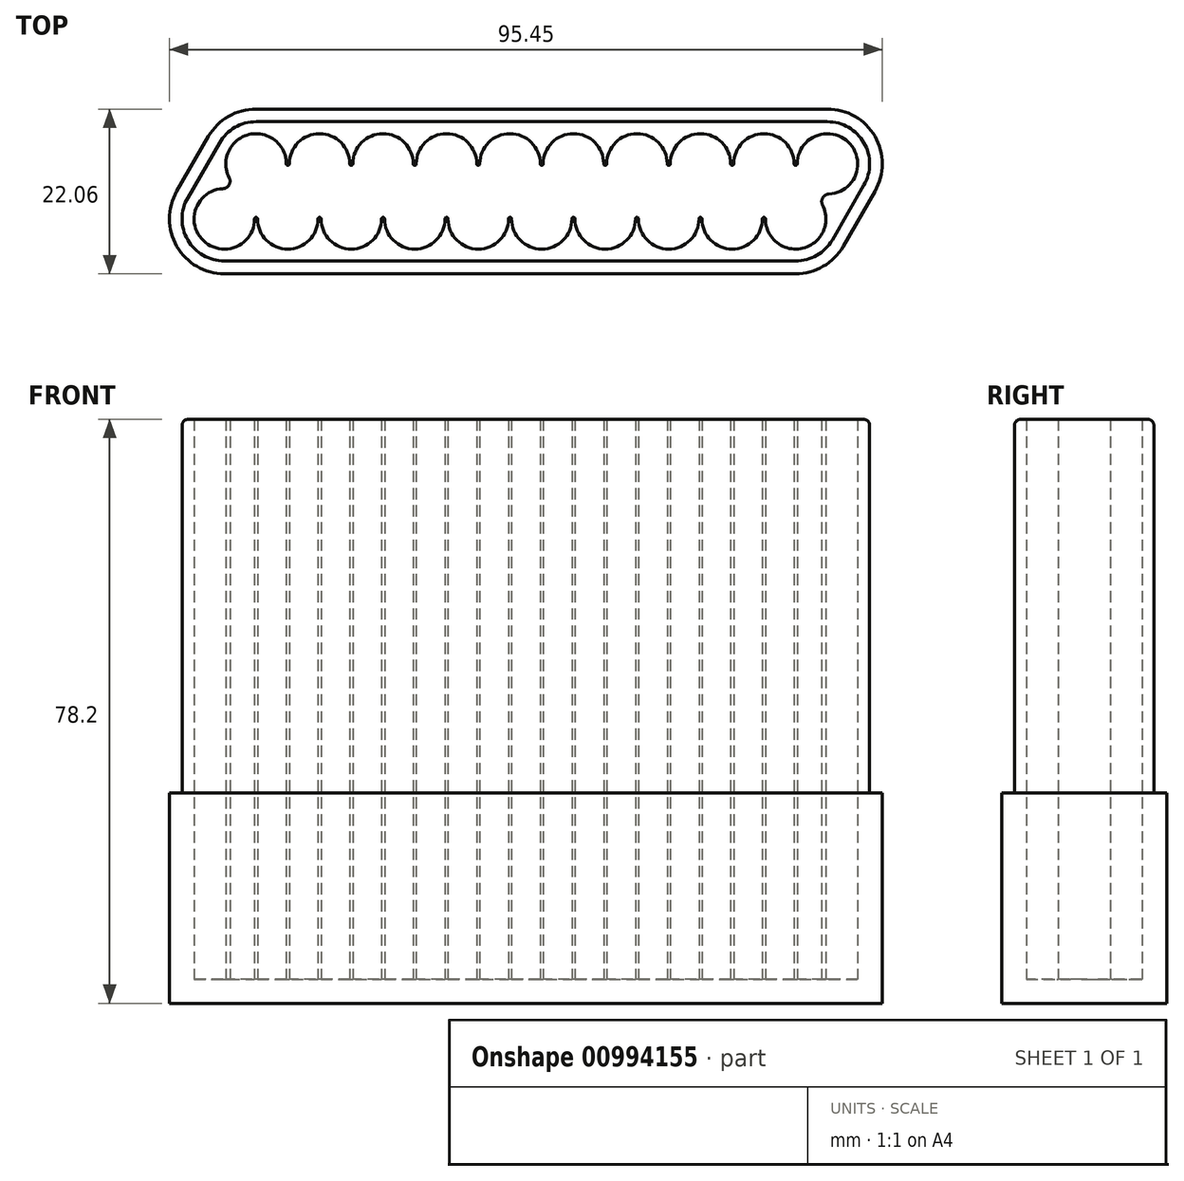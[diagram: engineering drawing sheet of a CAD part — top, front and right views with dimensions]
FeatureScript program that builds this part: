
annotation { "Feature Type Name" : "Feature", "Feature Type Description" : "" }
export const myFeature = defineFeature(function(context is Context, id is Id, definition is map)
    precondition{}
    {
        {
            var Q0;
            Q0=qCreatedBy(makeId("Top.planeOp"),FACE);
            var sketch = newSketch(context, id + "F0", { "sketchPlane" : qUnion([Q0])});
            skCircle(sketch, "E0", {"center": v(0, 0) * mm, "radius": 4.05 * mm});
            skCircle(sketch, "E1.0.1.0", {"center": v(4.25, 7.36) * mm, "radius": 4.05 * mm});
            skCircle(sketch, "E1.1.0.0", {"center": v(8.5, 0) * mm, "radius": 4.05 * mm});
            skCircle(sketch, "E1.1.1.0", {"center": v(12.75, 7.36) * mm, "radius": 4.05 * mm});
            skCircle(sketch, "E1.2.0.0", {"center": v(17, 0) * mm, "radius": 4.05 * mm});
            skCircle(sketch, "E1.2.1.0", {"center": v(21.25, 7.36) * mm, "radius": 4.05 * mm});
            skCircle(sketch, "E1.3.0.0", {"center": v(25.5, 0) * mm, "radius": 4.05 * mm});
            skCircle(sketch, "E1.3.1.0", {"center": v(29.75, 7.36) * mm, "radius": 4.05 * mm});
            skCircle(sketch, "E1.4.0.0", {"center": v(34, 0) * mm, "radius": 4.05 * mm});
            skCircle(sketch, "E1.4.1.0", {"center": v(38.25, 7.36) * mm, "radius": 4.05 * mm});
            skCircle(sketch, "E1.5.0.0", {"center": v(42.5, 0) * mm, "radius": 4.05 * mm});
            skCircle(sketch, "E1.5.1.0", {"center": v(46.75, 7.36) * mm, "radius": 4.05 * mm});
            skCircle(sketch, "E1.6.0.0", {"center": v(51, 0) * mm, "radius": 4.05 * mm});
            skCircle(sketch, "E1.6.1.0", {"center": v(55.25, 7.36) * mm, "radius": 4.05 * mm});
            skCircle(sketch, "E1.7.0.0", {"center": v(59.5, 0) * mm, "radius": 4.05 * mm});
            skCircle(sketch, "E1.7.1.0", {"center": v(63.75, 7.36) * mm, "radius": 4.05 * mm});
            skCircle(sketch, "E1.8.0.0", {"center": v(68, 0) * mm, "radius": 4.05 * mm});
            skCircle(sketch, "E1.8.1.0", {"center": v(72.25, 7.36) * mm, "radius": 4.05 * mm});
            skCircle(sketch, "E1.9.0.0", {"center": v(76.5, 0) * mm, "radius": 4.05 * mm});
            skCircle(sketch, "E1.9.1.0", {"center": v(80.75, 7.36) * mm, "radius": 4.05 * mm});
            skLineSegment(sketch, "E1.direction1", {"start": v(0, 0) * mm, "end": v(8.5, 0) * mm, "construction": true});
            skLineSegment(sketch, "E1.direction2", {"start": v(0, 0) * mm, "end": v(4.25, 7.36) * mm, "construction": true});
            skLineSegment(sketch, "E2", {"start": v(-6.37, 3.67) * mm, "end": v(-2.12, 11.04) * mm});
            skLineSegment(sketch, "E3", {"start": v(-4.9, 2.83) * mm, "end": v(-0.64, 10.19) * mm});
            skLineSegment(sketch, "E4", {"start": v(85.64, 4.54) * mm, "end": v(81.4, -2.82) * mm});
            skLineSegment(sketch, "E5", {"start": v(87.12, 3.69) * mm, "end": v(82.87, -3.67) * mm});
            skLineSegment(sketch, "E6", {"start": v(4.25, 13.01) * mm, "end": v(80.75, 13.01) * mm});
            skLineSegment(sketch, "E7", {"start": v(80.75, 14.71) * mm, "end": v(4.25, 14.71) * mm});
            skLineSegment(sketch, "E8", {"start": v(0, -5.65) * mm, "end": v(76.5, -5.65) * mm});
            skLineSegment(sketch, "E9", {"start": v(76.5, -7.35) * mm, "end": v(0, -7.35) * mm});
            skArc(sketch, "E10", {"start": v(-6.37, 3.67) * mm, "mid": v(-6.37, -3.68) * mm, "end": v(0, -7.35) * mm});
            skArc(sketch, "E11", {"start": v(0, -7.35) * mm, "mid": v(6.37, 3.68) * mm, "end": v(-6.37, 3.67) * mm, "construction": true});
            skArc(sketch, "E12", {"start": v(0, -5.65) * mm, "mid": v(4.9, 2.82) * mm, "end": v(-4.9, 2.83) * mm, "construction": true});
            skArc(sketch, "E13", {"start": v(-4.9, 2.83) * mm, "mid": v(-4.9, -2.83) * mm, "end": v(0, -5.65) * mm});
            skArc(sketch, "E14", {"start": v(4.25, 13.01) * mm, "mid": v(1.43, 12.25) * mm, "end": v(-0.64, 10.19) * mm});
            skArc(sketch, "E15", {"start": v(-0.64, 10.19) * mm, "mid": v(7.08, 2.47) * mm, "end": v(4.25, 13.01) * mm, "construction": true});
            skArc(sketch, "E16", {"start": v(-2.12, 11.04) * mm, "mid": v(7.93, 1) * mm, "end": v(4.25, 14.71) * mm, "construction": true});
            skArc(sketch, "E17", {"start": v(4.25, 14.71) * mm, "mid": v(0.58, 13.73) * mm, "end": v(-2.12, 11.04) * mm});
            skArc(sketch, "E18", {"start": v(80.75, 14.71) * mm, "mid": v(74.38, 3.69) * mm, "end": v(87.12, 3.69) * mm, "construction": true});
            skArc(sketch, "E19", {"start": v(87.12, 3.69) * mm, "mid": v(87.12, 11.04) * mm, "end": v(80.75, 14.71) * mm});
            skArc(sketch, "E20", {"start": v(85.64, 4.54) * mm, "mid": v(85.64, 10.19) * mm, "end": v(80.75, 13.01) * mm});
            skArc(sketch, "E21", {"start": v(80.75, 13.01) * mm, "mid": v(75.86, 4.54) * mm, "end": v(85.64, 4.54) * mm, "construction": true});
            skArc(sketch, "E22", {"start": v(82.87, -3.68) * mm, "mid": v(72.83, 6.37) * mm, "end": v(76.5, -7.35) * mm, "construction": true});
            skArc(sketch, "E23", {"start": v(76.5, -7.35) * mm, "mid": v(80.18, -6.37) * mm, "end": v(82.87, -3.68) * mm});
            skArc(sketch, "E24", {"start": v(76.5, -5.65) * mm, "mid": v(79.33, -4.9) * mm, "end": v(81.4, -2.82) * mm});
            skArc(sketch, "E25", {"start": v(81.4, -2.82) * mm, "mid": v(73.68, 4.9) * mm, "end": v(76.5, -5.65) * mm, "construction": true});
            skArc(sketch, "E26", {"start": v(4.45, 0) * mm, "mid": v(4.25, 0.2) * mm, "end": v(4.05, 0) * mm});
            skArc(sketch, "E27", {"start": v(4.05, 0) * mm, "mid": v(4.25, -0.2) * mm, "end": v(4.45, 0) * mm});
            skArc(sketch, "E28.0.1.0", {"start": v(8.7, 7.36) * mm, "mid": v(8.5, 7.56) * mm, "end": v(8.3, 7.36) * mm});
            skArc(sketch, "E28.0.1.1", {"start": v(8.3, 7.36) * mm, "mid": v(8.5, 7.16) * mm, "end": v(8.7, 7.36) * mm});
            skArc(sketch, "E28.1.0.0", {"start": v(12.95, 0) * mm, "mid": v(12.75, 0.2) * mm, "end": v(12.55, 0) * mm});
            skArc(sketch, "E28.1.0.1", {"start": v(12.55, 0) * mm, "mid": v(12.75, -0.2) * mm, "end": v(12.95, 0) * mm});
            skArc(sketch, "E28.1.1.0", {"start": v(17.2, 7.36) * mm, "mid": v(17, 7.56) * mm, "end": v(16.8, 7.36) * mm});
            skArc(sketch, "E28.1.1.1", {"start": v(16.8, 7.36) * mm, "mid": v(17, 7.16) * mm, "end": v(17.2, 7.36) * mm});
            skArc(sketch, "E28.2.0.0", {"start": v(21.45, 0) * mm, "mid": v(21.25, 0.2) * mm, "end": v(21.05, 0) * mm});
            skArc(sketch, "E28.2.0.1", {"start": v(21.05, 0) * mm, "mid": v(21.25, -0.2) * mm, "end": v(21.45, 0) * mm});
            skArc(sketch, "E28.2.1.0", {"start": v(25.7, 7.36) * mm, "mid": v(25.5, 7.56) * mm, "end": v(25.3, 7.36) * mm});
            skArc(sketch, "E28.2.1.1", {"start": v(25.3, 7.36) * mm, "mid": v(25.5, 7.16) * mm, "end": v(25.7, 7.36) * mm});
            skLineSegment(sketch, "E28.direction1", {"start": v(4.25, 0) * mm, "end": v(12.75, 0) * mm, "construction": true});
            skLineSegment(sketch, "E28.direction2", {"start": v(4.25, 0) * mm, "end": v(8.5, 7.36) * mm, "construction": true});
            skArc(sketch, "E29.0.3.0", {"start": v(29.95, 0) * mm, "mid": v(29.75, 0.2) * mm, "end": v(29.55, 0) * mm});
            skArc(sketch, "E29.4.3.0", {"start": v(29.55, 0) * mm, "mid": v(29.75, -0.2) * mm, "end": v(29.95, 0) * mm});
            skArc(sketch, "E29.0.3.1", {"start": v(34.2, 7.36) * mm, "mid": v(34, 7.56) * mm, "end": v(33.8, 7.36) * mm});
            skArc(sketch, "E29.4.3.1", {"start": v(33.8, 7.36) * mm, "mid": v(34, 7.16) * mm, "end": v(34.2, 7.36) * mm});
            skArc(sketch, "E29.0.4.0", {"start": v(38.45, 0) * mm, "mid": v(38.25, 0.2) * mm, "end": v(38.05, 0) * mm});
            skArc(sketch, "E29.4.4.0", {"start": v(38.05, 0) * mm, "mid": v(38.25, -0.2) * mm, "end": v(38.45, 0) * mm});
            skArc(sketch, "E29.0.4.1", {"start": v(42.7, 7.36) * mm, "mid": v(42.5, 7.56) * mm, "end": v(42.3, 7.36) * mm});
            skArc(sketch, "E29.4.4.1", {"start": v(42.3, 7.36) * mm, "mid": v(42.5, 7.16) * mm, "end": v(42.7, 7.36) * mm});
            skArc(sketch, "E29.0.5.0", {"start": v(46.95, 0) * mm, "mid": v(46.75, 0.2) * mm, "end": v(46.55, 0) * mm});
            skArc(sketch, "E29.4.5.0", {"start": v(46.55, 0) * mm, "mid": v(46.75, -0.2) * mm, "end": v(46.95, 0) * mm});
            skArc(sketch, "E29.0.5.1", {"start": v(51.2, 7.36) * mm, "mid": v(51, 7.56) * mm, "end": v(50.8, 7.36) * mm});
            skArc(sketch, "E29.4.5.1", {"start": v(50.8, 7.36) * mm, "mid": v(51, 7.16) * mm, "end": v(51.2, 7.36) * mm});
            skArc(sketch, "E29.0.6.0", {"start": v(55.45, 0) * mm, "mid": v(55.25, 0.2) * mm, "end": v(55.05, 0) * mm});
            skArc(sketch, "E29.4.6.0", {"start": v(55.05, 0) * mm, "mid": v(55.25, -0.2) * mm, "end": v(55.45, 0) * mm});
            skArc(sketch, "E29.0.6.1", {"start": v(59.7, 7.36) * mm, "mid": v(59.5, 7.56) * mm, "end": v(59.3, 7.36) * mm});
            skArc(sketch, "E29.4.6.1", {"start": v(59.3, 7.36) * mm, "mid": v(59.5, 7.16) * mm, "end": v(59.7, 7.36) * mm});
            skArc(sketch, "E29.0.7.0", {"start": v(63.95, 0) * mm, "mid": v(63.75, 0.2) * mm, "end": v(63.55, 0) * mm});
            skArc(sketch, "E29.4.7.0", {"start": v(63.55, 0) * mm, "mid": v(63.75, -0.2) * mm, "end": v(63.95, 0) * mm});
            skArc(sketch, "E29.0.7.1", {"start": v(68.2, 7.36) * mm, "mid": v(68, 7.56) * mm, "end": v(67.8, 7.36) * mm});
            skArc(sketch, "E29.4.7.1", {"start": v(67.8, 7.36) * mm, "mid": v(68, 7.16) * mm, "end": v(68.2, 7.36) * mm});
            skArc(sketch, "E29.0.8.0", {"start": v(72.45, 0) * mm, "mid": v(72.25, 0.2) * mm, "end": v(72.05, 0) * mm});
            skArc(sketch, "E29.4.8.0", {"start": v(72.05, 0) * mm, "mid": v(72.25, -0.2) * mm, "end": v(72.45, 0) * mm});
            skArc(sketch, "E29.0.8.1", {"start": v(76.7, 7.36) * mm, "mid": v(76.5, 7.56) * mm, "end": v(76.3, 7.36) * mm});
            skArc(sketch, "E29.4.8.1", {"start": v(76.3, 7.36) * mm, "mid": v(76.5, 7.16) * mm, "end": v(76.7, 7.36) * mm});
            skLineSegment(sketch, "E30", {"start": v(76.5, 0) * mm, "end": v(80.75, 7.36) * mm, "construction": true});
            skLineSegment(sketch, "E31", {"start": v(2.13, 3.68) * mm, "end": v(-0.24, 5.04) * mm, "construction": true});
            skArc(sketch, "E32", {"start": v(0.65, 5.5) * mm, "mid": v(-1.1, 5.54) * mm, "end": v(-0.2, 4.05) * mm, "construction": true});
            skArc(sketch, "E33", {"start": v(-0.2, 4.05) * mm, "mid": v(0.63, 4.54) * mm, "end": v(0.65, 5.5) * mm});
            skLineSegment(sketch, "E34", {"start": v(78.62, 3.68) * mm, "end": v(80.99, 2.32) * mm, "construction": true});
            skArc(sketch, "E35", {"start": v(80.94, 3.32) * mm, "mid": v(80.12, 2.82) * mm, "end": v(80.1, 1.86) * mm});
            skArc(sketch, "E36", {"start": v(80.1, 1.86) * mm, "mid": v(81.85, 1.82) * mm, "end": v(80.94, 3.32) * mm, "construction": true});
            skSolve(sketch);
        }
        {
            var Q0;
            Q0=makeQuery(id+"F0.imprint","IMPRINT",FACE,{"disambiguationData":[TD([[makeQuery(id+"F0.imprint","IMPRINT",EDGE,{"derivedFrom":sQuery(id+"F0.wireOp",EDGE,"E3")}),-1.0]])]});
            var Q1;
            Q1=makeQuery(id+"F0.imprint","IMPRINT",FACE,{"disambiguationData":[TD([[makeQuery(id+"F0.imprint","IMPRINT",EDGE,{"derivedFrom":sQuery(id+"F0.wireOp",EDGE,"E26")}),1.0]])]});
            var Q2;
            {var subQ0=sQuery(id+"F0.wireOp",EDGE,"E28.0.1.0");Q2=makeQuery(id+"F0.imprint","IMPRINT",FACE,{"disambiguationData":[TD([[makeQuery(id+"F0.imprint","IMPRINT",EDGE,{"derivedFrom":subQ0}),1.0]])]});}
            var Q3;
            Q3=makeQuery(id+"F0.imprint","IMPRINT",FACE,{"disambiguationData":[TD([[makeQuery(id+"F0.imprint","IMPRINT",EDGE,{"derivedFrom":sQuery(id+"F0.wireOp",EDGE,"E28.1.0.0")}),1.0]])]});
            var Q4;
            Q4=makeQuery(id+"F0.imprint","IMPRINT",FACE,{"disambiguationData":[TD([[makeQuery(id+"F0.imprint","IMPRINT",EDGE,{"derivedFrom":sQuery(id+"F0.wireOp",EDGE,"E28.1.1.0")}),1.0]])]});
            var Q5;
            Q5=makeQuery(id+"F0.imprint","IMPRINT",FACE,{"disambiguationData":[TD([[makeQuery(id+"F0.imprint","IMPRINT",EDGE,{"derivedFrom":sQuery(id+"F0.wireOp",EDGE,"E28.2.0.0")}),1.0]])]});
            var Q6;
            Q6=makeQuery(id+"F0.imprint","IMPRINT",FACE,{"disambiguationData":[TD([[makeQuery(id+"F0.imprint","IMPRINT",EDGE,{"derivedFrom":sQuery(id+"F0.wireOp",EDGE,"E28.2.1.0")}),1.0]])]});
            var Q7;
            Q7=makeQuery(id+"F0.imprint","IMPRINT",FACE,{"disambiguationData":[TD([[makeQuery(id+"F0.imprint","IMPRINT",EDGE,{"derivedFrom":sQuery(id+"F0.wireOp",EDGE,"E29.0.3.0")}),1.0]])]});
            var Q8;
            Q8=makeQuery(id+"F0.imprint","IMPRINT",FACE,{"disambiguationData":[TD([[makeQuery(id+"F0.imprint","IMPRINT",EDGE,{"derivedFrom":sQuery(id+"F0.wireOp",EDGE,"E29.0.3.1")}),1.0]])]});
            var Q9;
            Q9=makeQuery(id+"F0.imprint","IMPRINT",FACE,{"disambiguationData":[TD([[makeQuery(id+"F0.imprint","IMPRINT",EDGE,{"derivedFrom":sQuery(id+"F0.wireOp",EDGE,"E29.0.4.0")}),1.0]])]});
            var Q10;
            Q10=makeQuery(id+"F0.imprint","IMPRINT",FACE,{"disambiguationData":[TD([[makeQuery(id+"F0.imprint","IMPRINT",EDGE,{"derivedFrom":sQuery(id+"F0.wireOp",EDGE,"E29.0.4.1")}),1.0]])]});
            var Q11;
            Q11=makeQuery(id+"F0.imprint","IMPRINT",FACE,{"disambiguationData":[TD([[makeQuery(id+"F0.imprint","IMPRINT",EDGE,{"derivedFrom":sQuery(id+"F0.wireOp",EDGE,"E29.0.5.0")}),1.0]])]});
            var Q12;
            Q12=makeQuery(id+"F0.imprint","IMPRINT",FACE,{"disambiguationData":[TD([[makeQuery(id+"F0.imprint","IMPRINT",EDGE,{"derivedFrom":sQuery(id+"F0.wireOp",EDGE,"E29.0.5.1")}),1.0]])]});
            var Q13;
            Q13=makeQuery(id+"F0.imprint","IMPRINT",FACE,{"disambiguationData":[TD([[makeQuery(id+"F0.imprint","IMPRINT",EDGE,{"derivedFrom":sQuery(id+"F0.wireOp",EDGE,"E29.0.6.0")}),1.0]])]});
            var Q14;
            Q14=makeQuery(id+"F0.imprint","IMPRINT",FACE,{"disambiguationData":[TD([[makeQuery(id+"F0.imprint","IMPRINT",EDGE,{"derivedFrom":sQuery(id+"F0.wireOp",EDGE,"E29.0.6.1")}),1.0]])]});
            var Q15;
            Q15=makeQuery(id+"F0.imprint","IMPRINT",FACE,{"disambiguationData":[TD([[makeQuery(id+"F0.imprint","IMPRINT",EDGE,{"derivedFrom":sQuery(id+"F0.wireOp",EDGE,"E29.0.7.0")}),1.0]])]});
            var Q16;
            Q16=makeQuery(id+"F0.imprint","IMPRINT",FACE,{"disambiguationData":[TD([[makeQuery(id+"F0.imprint","IMPRINT",EDGE,{"derivedFrom":sQuery(id+"F0.wireOp",EDGE,"E29.0.7.1")}),1.0]])]});
            var Q17;
            Q17=makeQuery(id+"F0.imprint","IMPRINT",FACE,{"disambiguationData":[TD([[makeQuery(id+"F0.imprint","IMPRINT",EDGE,{"derivedFrom":sQuery(id+"F0.wireOp",EDGE,"E29.0.8.0")}),1.0]])]});
            var Q18;
            Q18=makeQuery(id+"F0.imprint","IMPRINT",FACE,{"disambiguationData":[TD([[makeQuery(id+"F0.imprint","IMPRINT",EDGE,{"derivedFrom":sQuery(id+"F0.wireOp",EDGE,"E29.0.8.1")}),1.0]])]});
            var Q19;
            Q19=makeQuery(id+"F0.imprint","IMPRINT",FACE,{"disambiguationData":[TD([[makeQuery(id+"F0.imprint","IMPRINT",EDGE,{"derivedFrom":sQuery(id+"F0.wireOp",EDGE,"E29.0.9.0")}),1.0]])]});
            var Q20;
            Q20=makeQuery(id+"F0.imprint","IMPRINT",FACE,{"disambiguationData":[TD([[makeQuery(id+"F0.imprint","IMPRINT",EDGE,{"derivedFrom":sQuery(id+"F0.wireOp",EDGE,"E29.0.9.1")}),1.0]])]});
            var Q21;
            Q21=makeQuery(id+"F0.imprint","IMPRINT",FACE,{"disambiguationData":[TD([[makeQuery(id+"F0.imprint","IMPRINT",EDGE,{"derivedFrom":sQuery(id+"F0.wireOp",EDGE,"E29.0.10.0")}),1.0]])]});
            var Q22;
            Q22=makeQuery(id+"F0.imprint","IMPRINT",FACE,{"disambiguationData":[TD([[makeQuery(id+"F0.imprint","IMPRINT",EDGE,{"derivedFrom":sQuery(id+"F0.wireOp",EDGE,"E29.0.10.1")}),1.0]])]});
            var Q23;
            Q23=makeQuery(id+"F0.imprint","IMPRINT",FACE,{"disambiguationData":[TD([[makeQuery(id+"F0.imprint","IMPRINT",EDGE,{"derivedFrom":sQuery(id+"F0.wireOp",EDGE,"E29.0.11.0")}),1.0]])]});
            var Q24;
            Q24=makeQuery(id+"F0.imprint","IMPRINT",FACE,{"disambiguationData":[TD([[makeQuery(id+"F0.imprint","IMPRINT",EDGE,{"derivedFrom":sQuery(id+"F0.wireOp",EDGE,"E29.0.11.1")}),1.0]])]});
            var Q25;
            Q25=makeQuery(id+"F0.imprint","IMPRINT",FACE,{"disambiguationData":[TD([[makeQuery(id+"F0.imprint","IMPRINT",EDGE,{"derivedFrom":sQuery(id+"F0.wireOp",EDGE,"E29.0.12.0")}),1.0]])]});
            var Q26;
            Q26=makeQuery(id+"F0.imprint","IMPRINT",FACE,{"disambiguationData":[TD([[makeQuery(id+"F0.imprint","IMPRINT",EDGE,{"derivedFrom":sQuery(id+"F0.wireOp",EDGE,"E29.0.12.1")}),1.0]])]});
            var Q27;
            Q27=makeQuery(id+"F0.imprint","IMPRINT",FACE,{"disambiguationData":[TD([[makeQuery(id+"F0.imprint","IMPRINT",EDGE,{"derivedFrom":sQuery(id+"F0.wireOp",EDGE,"E29.0.13.0")}),1.0]])]});
            var Q28;
            Q28=makeQuery(id+"F0.imprint","IMPRINT",FACE,{"disambiguationData":[TD([[makeQuery(id+"F0.imprint","IMPRINT",EDGE,{"derivedFrom":sQuery(id+"F0.wireOp",EDGE,"E29.0.13.1")}),1.0]])]});
            var Q29;
            Q29=makeQuery(id+"F0.imprint","IMPRINT",FACE,{"disambiguationData":[TD([[makeQuery(id+"F0.imprint","IMPRINT",EDGE,{"derivedFrom":sQuery(id+"F0.wireOp",EDGE,"E29.0.14.0")}),1.0]])]});
            var Q30;
            Q30=makeQuery(id+"F0.imprint","IMPRINT",FACE,{"disambiguationData":[TD([[makeQuery(id+"F0.imprint","IMPRINT",EDGE,{"derivedFrom":sQuery(id+"F0.wireOp",EDGE,"E29.0.14.1")}),1.0]])]});
            var Q31;
            Q31=makeQuery(id+"F0.imprint","IMPRINT",FACE,{"disambiguationData":[TD([[makeQuery(id+"F0.imprint","IMPRINT",EDGE,{"derivedFrom":sQuery(id+"F0.wireOp",EDGE,"E29.0.15.0")}),1.0]])]});
            var Q32;
            Q32=makeQuery(id+"F0.imprint","IMPRINT",FACE,{"disambiguationData":[TD([[makeQuery(id+"F0.imprint","IMPRINT",EDGE,{"derivedFrom":sQuery(id+"F0.wireOp",EDGE,"E29.0.15.1")}),1.0]])]});
            var Q33;
            Q33=makeQuery(id+"F0.imprint","IMPRINT",FACE,{"disambiguationData":[TD([[makeQuery(id+"F0.imprint","IMPRINT",EDGE,{"derivedFrom":sQuery(id+"F0.wireOp",EDGE,"E29.0.16.0")}),1.0]])]});
            var Q34;
            Q34=makeQuery(id+"F0.imprint","IMPRINT",FACE,{"disambiguationData":[TD([[makeQuery(id+"F0.imprint","IMPRINT",EDGE,{"derivedFrom":sQuery(id+"F0.wireOp",EDGE,"E29.0.16.1")}),1.0]])]});
            var Q35;
            Q35=makeQuery(id+"F0.imprint","IMPRINT",FACE,{"disambiguationData":[TD([[makeQuery(id+"F0.imprint","IMPRINT",EDGE,{"derivedFrom":sQuery(id+"F0.wireOp",EDGE,"E29.0.17.0")}),1.0]])]});
            var Q36;
            Q36=makeQuery(id+"F0.imprint","IMPRINT",FACE,{"disambiguationData":[TD([[makeQuery(id+"F0.imprint","IMPRINT",EDGE,{"derivedFrom":sQuery(id+"F0.wireOp",EDGE,"E29.0.17.1")}),1.0]])]});
            var Q37;
            Q37=makeQuery(id+"F0.imprint","IMPRINT",FACE,{"disambiguationData":[TD([[makeQuery(id+"F0.imprint","IMPRINT",EDGE,{"derivedFrom":sQuery(id+"F0.wireOp",EDGE,"E29.0.18.0")}),1.0]])]});
            var Q38;
            Q38=makeQuery(id+"F0.imprint","IMPRINT",FACE,{"disambiguationData":[TD([[makeQuery(id+"F0.imprint","IMPRINT",EDGE,{"derivedFrom":sQuery(id+"F0.wireOp",EDGE,"E29.0.18.1")}),1.0]])]});
            extrude(context, id + "F1", {"entities" : qUnion([Q0, Q1, Q2, Q3, Q4, Q5, Q6, Q7, Q8, Q9, Q10, Q11, Q12, Q13, Q14, Q15, Q16, Q17, Q18, Q19, Q20, Q21, Q22, Q23, Q24, Q25, Q26, Q27, Q28, Q29, Q30, Q31, Q32, Q33, Q34, Q35, Q36, Q37, Q38]), "depth" : 75 * mm, "offsetDistance" : 25 * mm});
        }
        {
            var Q0;
            Q0=makeQuery(id+"F0.imprint","IMPRINT",FACE,{"disambiguationData":[TD([[makeQuery(id+"F0.imprint","IMPRINT",EDGE,{"derivedFrom":sQuery(id+"F0.wireOp",EDGE,"a81a9441-913f-4e04-ae89-87223a70fdbe.0")}),1.0]])]});
            var Q1;
            Q1=makeQuery(id+"F0.imprint","IMPRINT",FACE,{"disambiguationData":[TD([[makeQuery(id+"F0.imprint","IMPRINT",EDGE,{"derivedFrom":sQuery(id+"F0.wireOp",EDGE,"E2")}),-1.0]])]});
            extrude(context, id + "F2", {"entities" : qUnion([Q0, Q1]), "operationType" : NewBodyOperationType.ADD, "depth" : 25 * mm, "offsetDistance" : 25 * mm});
        }
        {
            var Q0;
            Q0=qSketchRegion(id+"F0",true);
            var Q1;
            Q1=makeQuery(id+"F0.imprint","IMPRINT",FACE,{"disambiguationData":[TD([[makeQuery(id+"F0.imprint","IMPRINT",EDGE,{"derivedFrom":sQuery(id+"F0.wireOp",EDGE,"E3")}),-1.0]])]});
            var Q2;
            {var subQ50=sQuery(id+"F0.wireOp",EDGE,"f7ba4f12-d8f7-416d-8bb5-9bc70fdc84212");Q2=makeQuery(id+"F0.imprint","IMPRINT",FACE,{"disambiguationData":[TD([[makeQuery(id+"F0.imprint","IMPRINT",EDGE,{"derivedFrom":subQ50}),-1.0]])]});}
            var Q3;
            {var subQ0=sQuery(id+"F0.wireOp",EDGE,"E0");var subQ1=makeQuery(id+"F0.imprint","INTERSECT",VERTEX,{"derivedFrom":[subQ0,sQuery(id+"F0.wireOp",EDGE,"f7ba4f12-d8f7-416d-8bb5-9bc70fdc84212")]});Q3=makeQuery(id+"F0.imprint","IMPRINT",FACE,{"disambiguationData":[TD([[makeQuery(id+"F0.imprint","IMPRINT",EDGE,{"disambiguationData":[TD([[subQ1,1.0]])],"derivedFrom":subQ0}),1.0]])]});}
            var Q4;
            {var subQ0=sQuery(id+"F0.wireOp",EDGE,"E1.0.1.0");var subQ1=makeQuery(id+"F0.imprint","INTERSECT",VERTEX,{"derivedFrom":[subQ0,sQuery(id+"F0.wireOp",EDGE,"f7ba4f12-d8f7-416d-8bb5-9bc70fdc84212")]});Q4=makeQuery(id+"F0.imprint","IMPRINT",FACE,{"disambiguationData":[TD([[makeQuery(id+"F0.imprint","IMPRINT",EDGE,{"disambiguationData":[TD([[subQ1,1.0]])],"derivedFrom":subQ0}),1.0]])]});}
            var Q5;
            {var subQ0=sQuery(id+"F0.wireOp",EDGE,"E1.1.0.0");var subQ1=makeQuery(id+"F0.imprint","INTERSECT",VERTEX,{"derivedFrom":[subQ0,sQuery(id+"F0.wireOp",EDGE,"E26")]});Q5=makeQuery(id+"F0.imprint","IMPRINT",FACE,{"disambiguationData":[TD([[makeQuery(id+"F0.imprint","IMPRINT",EDGE,{"disambiguationData":[TD([[subQ1,1.0]])],"derivedFrom":subQ0}),1.0]])]});}
            var Q6;
            {var subQ0=sQuery(id+"F0.wireOp",EDGE,"E1.1.1.0");var subQ1=makeQuery(id+"F0.imprint","INTERSECT",VERTEX,{"derivedFrom":[subQ0,sQuery(id+"F0.wireOp",EDGE,"E28.0.1.1")]});Q6=makeQuery(id+"F0.imprint","IMPRINT",FACE,{"disambiguationData":[TD([[makeQuery(id+"F0.imprint","IMPRINT",EDGE,{"disambiguationData":[TD([[subQ1,1.0]])],"derivedFrom":subQ0}),1.0]])]});}
            var Q7;
            {var subQ0=sQuery(id+"F0.wireOp",EDGE,"E1.2.0.0");var subQ1=makeQuery(id+"F0.imprint","INTERSECT",VERTEX,{"derivedFrom":[subQ0,sQuery(id+"F0.wireOp",EDGE,"E28.1.0.0")]});Q7=makeQuery(id+"F0.imprint","IMPRINT",FACE,{"disambiguationData":[TD([[makeQuery(id+"F0.imprint","IMPRINT",EDGE,{"disambiguationData":[TD([[subQ1,1.0]])],"derivedFrom":subQ0}),1.0]])]});}
            var Q8;
            {var subQ0=sQuery(id+"F0.wireOp",EDGE,"E1.2.1.0");var subQ1=makeQuery(id+"F0.imprint","INTERSECT",VERTEX,{"derivedFrom":[subQ0,sQuery(id+"F0.wireOp",EDGE,"E28.1.1.1")]});Q8=makeQuery(id+"F0.imprint","IMPRINT",FACE,{"disambiguationData":[TD([[makeQuery(id+"F0.imprint","IMPRINT",EDGE,{"disambiguationData":[TD([[subQ1,1.0]])],"derivedFrom":subQ0}),1.0]])]});}
            var Q9;
            {var subQ0=sQuery(id+"F0.wireOp",EDGE,"E1.3.0.0");var subQ1=makeQuery(id+"F0.imprint","INTERSECT",VERTEX,{"derivedFrom":[subQ0,sQuery(id+"F0.wireOp",EDGE,"E28.2.0.0")]});Q9=makeQuery(id+"F0.imprint","IMPRINT",FACE,{"disambiguationData":[TD([[makeQuery(id+"F0.imprint","IMPRINT",EDGE,{"disambiguationData":[TD([[subQ1,1.0]])],"derivedFrom":subQ0}),1.0]])]});}
            var Q10;
            {var subQ0=sQuery(id+"F0.wireOp",EDGE,"E1.3.1.0");var subQ1=makeQuery(id+"F0.imprint","INTERSECT",VERTEX,{"derivedFrom":[subQ0,sQuery(id+"F0.wireOp",EDGE,"E28.2.1.1")]});Q10=makeQuery(id+"F0.imprint","IMPRINT",FACE,{"disambiguationData":[TD([[makeQuery(id+"F0.imprint","IMPRINT",EDGE,{"disambiguationData":[TD([[subQ1,1.0]])],"derivedFrom":subQ0}),1.0]])]});}
            var Q11;
            {var subQ0=sQuery(id+"F0.wireOp",EDGE,"E1.4.0.0");var subQ1=makeQuery(id+"F0.imprint","INTERSECT",VERTEX,{"derivedFrom":[subQ0,sQuery(id+"F0.wireOp",EDGE,"E29.0.3.0")]});Q11=makeQuery(id+"F0.imprint","IMPRINT",FACE,{"disambiguationData":[TD([[makeQuery(id+"F0.imprint","IMPRINT",EDGE,{"disambiguationData":[TD([[subQ1,1.0]])],"derivedFrom":subQ0}),1.0]])]});}
            var Q12;
            {var subQ0=sQuery(id+"F0.wireOp",EDGE,"E1.4.1.0");var subQ1=makeQuery(id+"F0.imprint","INTERSECT",VERTEX,{"derivedFrom":[subQ0,sQuery(id+"F0.wireOp",EDGE,"E29.4.3.1")]});Q12=makeQuery(id+"F0.imprint","IMPRINT",FACE,{"disambiguationData":[TD([[makeQuery(id+"F0.imprint","IMPRINT",EDGE,{"disambiguationData":[TD([[subQ1,1.0]])],"derivedFrom":subQ0}),1.0]])]});}
            var Q13;
            {var subQ0=sQuery(id+"F0.wireOp",EDGE,"E1.5.0.0");var subQ1=makeQuery(id+"F0.imprint","INTERSECT",VERTEX,{"derivedFrom":[subQ0,sQuery(id+"F0.wireOp",EDGE,"E29.0.4.0")]});Q13=makeQuery(id+"F0.imprint","IMPRINT",FACE,{"disambiguationData":[TD([[makeQuery(id+"F0.imprint","IMPRINT",EDGE,{"disambiguationData":[TD([[subQ1,1.0]])],"derivedFrom":subQ0}),1.0]])]});}
            var Q14;
            {var subQ0=sQuery(id+"F0.wireOp",EDGE,"E1.5.1.0");var subQ1=makeQuery(id+"F0.imprint","INTERSECT",VERTEX,{"derivedFrom":[subQ0,sQuery(id+"F0.wireOp",EDGE,"E29.4.4.1")]});Q14=makeQuery(id+"F0.imprint","IMPRINT",FACE,{"disambiguationData":[TD([[makeQuery(id+"F0.imprint","IMPRINT",EDGE,{"disambiguationData":[TD([[subQ1,1.0]])],"derivedFrom":subQ0}),1.0]])]});}
            var Q15;
            {var subQ0=sQuery(id+"F0.wireOp",EDGE,"E1.6.0.0");var subQ1=makeQuery(id+"F0.imprint","INTERSECT",VERTEX,{"derivedFrom":[subQ0,sQuery(id+"F0.wireOp",EDGE,"E29.0.5.0")]});Q15=makeQuery(id+"F0.imprint","IMPRINT",FACE,{"disambiguationData":[TD([[makeQuery(id+"F0.imprint","IMPRINT",EDGE,{"disambiguationData":[TD([[subQ1,1.0]])],"derivedFrom":subQ0}),1.0]])]});}
            var Q16;
            {var subQ0=sQuery(id+"F0.wireOp",EDGE,"E1.6.1.0");var subQ1=makeQuery(id+"F0.imprint","INTERSECT",VERTEX,{"derivedFrom":[subQ0,sQuery(id+"F0.wireOp",EDGE,"E29.4.5.1")]});Q16=makeQuery(id+"F0.imprint","IMPRINT",FACE,{"disambiguationData":[TD([[makeQuery(id+"F0.imprint","IMPRINT",EDGE,{"disambiguationData":[TD([[subQ1,1.0]])],"derivedFrom":subQ0}),1.0]])]});}
            var Q17;
            {var subQ0=sQuery(id+"F0.wireOp",EDGE,"E1.7.0.0");var subQ1=makeQuery(id+"F0.imprint","INTERSECT",VERTEX,{"derivedFrom":[subQ0,sQuery(id+"F0.wireOp",EDGE,"E29.0.6.0")]});Q17=makeQuery(id+"F0.imprint","IMPRINT",FACE,{"disambiguationData":[TD([[makeQuery(id+"F0.imprint","IMPRINT",EDGE,{"disambiguationData":[TD([[subQ1,1.0]])],"derivedFrom":subQ0}),1.0]])]});}
            var Q18;
            {var subQ0=sQuery(id+"F0.wireOp",EDGE,"E1.7.1.0");var subQ1=makeQuery(id+"F0.imprint","INTERSECT",VERTEX,{"derivedFrom":[subQ0,sQuery(id+"F0.wireOp",EDGE,"E29.4.6.1")]});Q18=makeQuery(id+"F0.imprint","IMPRINT",FACE,{"disambiguationData":[TD([[makeQuery(id+"F0.imprint","IMPRINT",EDGE,{"disambiguationData":[TD([[subQ1,1.0]])],"derivedFrom":subQ0}),1.0]])]});}
            var Q19;
            {var subQ0=sQuery(id+"F0.wireOp",EDGE,"E1.8.0.0");var subQ1=makeQuery(id+"F0.imprint","INTERSECT",VERTEX,{"derivedFrom":[subQ0,sQuery(id+"F0.wireOp",EDGE,"E29.0.7.0")]});Q19=makeQuery(id+"F0.imprint","IMPRINT",FACE,{"disambiguationData":[TD([[makeQuery(id+"F0.imprint","IMPRINT",EDGE,{"disambiguationData":[TD([[subQ1,1.0]])],"derivedFrom":subQ0}),1.0]])]});}
            var Q20;
            {var subQ0=sQuery(id+"F0.wireOp",EDGE,"E1.8.1.0");var subQ1=makeQuery(id+"F0.imprint","INTERSECT",VERTEX,{"derivedFrom":[subQ0,sQuery(id+"F0.wireOp",EDGE,"E29.4.7.1")]});Q20=makeQuery(id+"F0.imprint","IMPRINT",FACE,{"disambiguationData":[TD([[makeQuery(id+"F0.imprint","IMPRINT",EDGE,{"disambiguationData":[TD([[subQ1,1.0]])],"derivedFrom":subQ0}),1.0]])]});}
            var Q21;
            {var subQ0=sQuery(id+"F0.wireOp",EDGE,"E1.9.0.0");var subQ1=makeQuery(id+"F0.imprint","INTERSECT",VERTEX,{"derivedFrom":[subQ0,sQuery(id+"F0.wireOp",EDGE,"E29.0.8.0")]});Q21=makeQuery(id+"F0.imprint","IMPRINT",FACE,{"disambiguationData":[TD([[makeQuery(id+"F0.imprint","IMPRINT",EDGE,{"disambiguationData":[TD([[subQ1,1.0]])],"derivedFrom":subQ0}),1.0]])]});}
            var Q22;
            {var subQ0=sQuery(id+"F0.wireOp",EDGE,"E1.9.1.0");var subQ1=makeQuery(id+"F0.imprint","INTERSECT",VERTEX,{"derivedFrom":[subQ0,sQuery(id+"F0.wireOp",EDGE,"E29.4.8.1")]});Q22=makeQuery(id+"F0.imprint","IMPRINT",FACE,{"disambiguationData":[TD([[makeQuery(id+"F0.imprint","IMPRINT",EDGE,{"disambiguationData":[TD([[subQ1,1.0]])],"derivedFrom":subQ0}),1.0]])]});}
            var Q23;
            {var subQ0=sQuery(id+"F0.wireOp",EDGE,"bb5cbe6f-1803-4565-ad2e-bfdc8dac2585.0.10.0");var subQ1=makeQuery(id+"F0.imprint","INTERSECT",VERTEX,{"derivedFrom":[subQ0,sQuery(id+"F0.wireOp",EDGE,"E29.0.9.0")]});Q23=makeQuery(id+"F0.imprint","IMPRINT",FACE,{"disambiguationData":[TD([[makeQuery(id+"F0.imprint","IMPRINT",EDGE,{"disambiguationData":[TD([[subQ1,1.0]])],"derivedFrom":subQ0}),1.0]])]});}
            var Q24;
            {var subQ0=sQuery(id+"F0.wireOp",EDGE,"bb5cbe6f-1803-4565-ad2e-bfdc8dac2585.0.10.1");var subQ1=makeQuery(id+"F0.imprint","INTERSECT",VERTEX,{"derivedFrom":[subQ0,sQuery(id+"F0.wireOp",EDGE,"E29.4.9.1")]});Q24=makeQuery(id+"F0.imprint","IMPRINT",FACE,{"disambiguationData":[TD([[makeQuery(id+"F0.imprint","IMPRINT",EDGE,{"disambiguationData":[TD([[subQ1,1.0]])],"derivedFrom":subQ0}),1.0]])]});}
            var Q25;
            {var subQ0=sQuery(id+"F0.wireOp",EDGE,"bb5cbe6f-1803-4565-ad2e-bfdc8dac2585.0.11.0");var subQ1=makeQuery(id+"F0.imprint","INTERSECT",VERTEX,{"derivedFrom":[subQ0,sQuery(id+"F0.wireOp",EDGE,"E29.0.10.0")]});Q25=makeQuery(id+"F0.imprint","IMPRINT",FACE,{"disambiguationData":[TD([[makeQuery(id+"F0.imprint","IMPRINT",EDGE,{"disambiguationData":[TD([[subQ1,1.0]])],"derivedFrom":subQ0}),1.0]])]});}
            var Q26;
            {var subQ0=sQuery(id+"F0.wireOp",EDGE,"bb5cbe6f-1803-4565-ad2e-bfdc8dac2585.0.11.1");var subQ1=makeQuery(id+"F0.imprint","INTERSECT",VERTEX,{"derivedFrom":[subQ0,sQuery(id+"F0.wireOp",EDGE,"E29.4.10.1")]});Q26=makeQuery(id+"F0.imprint","IMPRINT",FACE,{"disambiguationData":[TD([[makeQuery(id+"F0.imprint","IMPRINT",EDGE,{"disambiguationData":[TD([[subQ1,1.0]])],"derivedFrom":subQ0}),1.0]])]});}
            var Q27;
            {var subQ0=sQuery(id+"F0.wireOp",EDGE,"bb5cbe6f-1803-4565-ad2e-bfdc8dac2585.0.12.0");var subQ1=makeQuery(id+"F0.imprint","INTERSECT",VERTEX,{"derivedFrom":[subQ0,sQuery(id+"F0.wireOp",EDGE,"E29.0.11.0")]});Q27=makeQuery(id+"F0.imprint","IMPRINT",FACE,{"disambiguationData":[TD([[makeQuery(id+"F0.imprint","IMPRINT",EDGE,{"disambiguationData":[TD([[subQ1,1.0]])],"derivedFrom":subQ0}),1.0]])]});}
            var Q28;
            {var subQ0=sQuery(id+"F0.wireOp",EDGE,"bb5cbe6f-1803-4565-ad2e-bfdc8dac2585.0.12.1");var subQ1=makeQuery(id+"F0.imprint","INTERSECT",VERTEX,{"derivedFrom":[subQ0,sQuery(id+"F0.wireOp",EDGE,"E29.4.11.1")]});Q28=makeQuery(id+"F0.imprint","IMPRINT",FACE,{"disambiguationData":[TD([[makeQuery(id+"F0.imprint","IMPRINT",EDGE,{"disambiguationData":[TD([[subQ1,1.0]])],"derivedFrom":subQ0}),1.0]])]});}
            var Q29;
            {var subQ0=sQuery(id+"F0.wireOp",EDGE,"bb5cbe6f-1803-4565-ad2e-bfdc8dac2585.0.13.0");var subQ1=makeQuery(id+"F0.imprint","INTERSECT",VERTEX,{"derivedFrom":[subQ0,sQuery(id+"F0.wireOp",EDGE,"E29.0.12.0")]});Q29=makeQuery(id+"F0.imprint","IMPRINT",FACE,{"disambiguationData":[TD([[makeQuery(id+"F0.imprint","IMPRINT",EDGE,{"disambiguationData":[TD([[subQ1,1.0]])],"derivedFrom":subQ0}),1.0]])]});}
            var Q30;
            {var subQ0=sQuery(id+"F0.wireOp",EDGE,"bb5cbe6f-1803-4565-ad2e-bfdc8dac2585.0.13.1");var subQ1=makeQuery(id+"F0.imprint","INTERSECT",VERTEX,{"derivedFrom":[subQ0,sQuery(id+"F0.wireOp",EDGE,"E29.4.12.1")]});Q30=makeQuery(id+"F0.imprint","IMPRINT",FACE,{"disambiguationData":[TD([[makeQuery(id+"F0.imprint","IMPRINT",EDGE,{"disambiguationData":[TD([[subQ1,1.0]])],"derivedFrom":subQ0}),1.0]])]});}
            var Q31;
            {var subQ0=sQuery(id+"F0.wireOp",EDGE,"bb5cbe6f-1803-4565-ad2e-bfdc8dac2585.0.14.0");var subQ1=makeQuery(id+"F0.imprint","INTERSECT",VERTEX,{"derivedFrom":[subQ0,sQuery(id+"F0.wireOp",EDGE,"E29.0.13.0")]});Q31=makeQuery(id+"F0.imprint","IMPRINT",FACE,{"disambiguationData":[TD([[makeQuery(id+"F0.imprint","IMPRINT",EDGE,{"disambiguationData":[TD([[subQ1,1.0]])],"derivedFrom":subQ0}),1.0]])]});}
            var Q32;
            {var subQ0=sQuery(id+"F0.wireOp",EDGE,"bb5cbe6f-1803-4565-ad2e-bfdc8dac2585.0.14.1");var subQ1=makeQuery(id+"F0.imprint","INTERSECT",VERTEX,{"derivedFrom":[subQ0,sQuery(id+"F0.wireOp",EDGE,"E29.4.13.1")]});Q32=makeQuery(id+"F0.imprint","IMPRINT",FACE,{"disambiguationData":[TD([[makeQuery(id+"F0.imprint","IMPRINT",EDGE,{"disambiguationData":[TD([[subQ1,1.0]])],"derivedFrom":subQ0}),1.0]])]});}
            var Q33;
            {var subQ0=sQuery(id+"F0.wireOp",EDGE,"bb5cbe6f-1803-4565-ad2e-bfdc8dac2585.0.15.0");var subQ1=makeQuery(id+"F0.imprint","INTERSECT",VERTEX,{"derivedFrom":[subQ0,sQuery(id+"F0.wireOp",EDGE,"E29.0.14.0")]});Q33=makeQuery(id+"F0.imprint","IMPRINT",FACE,{"disambiguationData":[TD([[makeQuery(id+"F0.imprint","IMPRINT",EDGE,{"disambiguationData":[TD([[subQ1,1.0]])],"derivedFrom":subQ0}),1.0]])]});}
            var Q34;
            {var subQ0=sQuery(id+"F0.wireOp",EDGE,"bb5cbe6f-1803-4565-ad2e-bfdc8dac2585.0.15.1");var subQ1=makeQuery(id+"F0.imprint","INTERSECT",VERTEX,{"derivedFrom":[subQ0,sQuery(id+"F0.wireOp",EDGE,"E29.4.14.1")]});Q34=makeQuery(id+"F0.imprint","IMPRINT",FACE,{"disambiguationData":[TD([[makeQuery(id+"F0.imprint","IMPRINT",EDGE,{"disambiguationData":[TD([[subQ1,1.0]])],"derivedFrom":subQ0}),1.0]])]});}
            var Q35;
            {var subQ0=sQuery(id+"F0.wireOp",EDGE,"bb5cbe6f-1803-4565-ad2e-bfdc8dac2585.0.16.0");var subQ1=makeQuery(id+"F0.imprint","INTERSECT",VERTEX,{"derivedFrom":[subQ0,sQuery(id+"F0.wireOp",EDGE,"E29.0.15.0")]});Q35=makeQuery(id+"F0.imprint","IMPRINT",FACE,{"disambiguationData":[TD([[makeQuery(id+"F0.imprint","IMPRINT",EDGE,{"disambiguationData":[TD([[subQ1,1.0]])],"derivedFrom":subQ0}),1.0]])]});}
            var Q36;
            {var subQ0=sQuery(id+"F0.wireOp",EDGE,"bb5cbe6f-1803-4565-ad2e-bfdc8dac2585.0.16.1");var subQ1=makeQuery(id+"F0.imprint","INTERSECT",VERTEX,{"derivedFrom":[subQ0,sQuery(id+"F0.wireOp",EDGE,"E29.4.15.1")]});Q36=makeQuery(id+"F0.imprint","IMPRINT",FACE,{"disambiguationData":[TD([[makeQuery(id+"F0.imprint","IMPRINT",EDGE,{"disambiguationData":[TD([[subQ1,1.0]])],"derivedFrom":subQ0}),1.0]])]});}
            var Q37;
            {var subQ0=sQuery(id+"F0.wireOp",EDGE,"bb5cbe6f-1803-4565-ad2e-bfdc8dac2585.0.17.0");var subQ1=makeQuery(id+"F0.imprint","INTERSECT",VERTEX,{"derivedFrom":[subQ0,sQuery(id+"F0.wireOp",EDGE,"E29.0.16.0")]});Q37=makeQuery(id+"F0.imprint","IMPRINT",FACE,{"disambiguationData":[TD([[makeQuery(id+"F0.imprint","IMPRINT",EDGE,{"disambiguationData":[TD([[subQ1,1.0]])],"derivedFrom":subQ0}),1.0]])]});}
            var Q38;
            {var subQ0=sQuery(id+"F0.wireOp",EDGE,"bb5cbe6f-1803-4565-ad2e-bfdc8dac2585.0.17.1");var subQ1=makeQuery(id+"F0.imprint","INTERSECT",VERTEX,{"derivedFrom":[subQ0,sQuery(id+"F0.wireOp",EDGE,"E29.4.16.1")]});Q38=makeQuery(id+"F0.imprint","IMPRINT",FACE,{"disambiguationData":[TD([[makeQuery(id+"F0.imprint","IMPRINT",EDGE,{"disambiguationData":[TD([[subQ1,1.0]])],"derivedFrom":subQ0}),1.0]])]});}
            var Q39;
            {var subQ0=sQuery(id+"F0.wireOp",EDGE,"bb5cbe6f-1803-4565-ad2e-bfdc8dac2585.0.18.0");var subQ1=makeQuery(id+"F0.imprint","INTERSECT",VERTEX,{"derivedFrom":[subQ0,sQuery(id+"F0.wireOp",EDGE,"E29.0.17.0")]});Q39=makeQuery(id+"F0.imprint","IMPRINT",FACE,{"disambiguationData":[TD([[makeQuery(id+"F0.imprint","IMPRINT",EDGE,{"disambiguationData":[TD([[subQ1,1.0]])],"derivedFrom":subQ0}),1.0]])]});}
            var Q40;
            {var subQ0=sQuery(id+"F0.wireOp",EDGE,"bb5cbe6f-1803-4565-ad2e-bfdc8dac2585.0.18.1");var subQ1=makeQuery(id+"F0.imprint","INTERSECT",VERTEX,{"derivedFrom":[subQ0,sQuery(id+"F0.wireOp",EDGE,"E29.4.17.1")]});Q40=makeQuery(id+"F0.imprint","IMPRINT",FACE,{"disambiguationData":[TD([[makeQuery(id+"F0.imprint","IMPRINT",EDGE,{"disambiguationData":[TD([[subQ1,1.0]])],"derivedFrom":subQ0}),1.0]])]});}
            var Q41;
            {var subQ0=sQuery(id+"F0.wireOp",EDGE,"bb5cbe6f-1803-4565-ad2e-bfdc8dac2585.0.19.0");var subQ1=makeQuery(id+"F0.imprint","INTERSECT",VERTEX,{"derivedFrom":[subQ0,sQuery(id+"F0.wireOp",EDGE,"E29.0.18.0")]});Q41=makeQuery(id+"F0.imprint","IMPRINT",FACE,{"disambiguationData":[TD([[makeQuery(id+"F0.imprint","IMPRINT",EDGE,{"disambiguationData":[TD([[subQ1,1.0]])],"derivedFrom":subQ0}),1.0]])]});}
            var Q42;
            {var subQ0=sQuery(id+"F0.wireOp",EDGE,"bb5cbe6f-1803-4565-ad2e-bfdc8dac2585.0.19.1");var subQ1=makeQuery(id+"F0.imprint","INTERSECT",VERTEX,{"derivedFrom":[subQ0,sQuery(id+"F0.wireOp",EDGE,"E29.4.18.1")]});Q42=makeQuery(id+"F0.imprint","IMPRINT",FACE,{"disambiguationData":[TD([[makeQuery(id+"F0.imprint","IMPRINT",EDGE,{"disambiguationData":[TD([[subQ1,-1.0]])],"derivedFrom":subQ0}),1.0]])]});}
            var Q43;
            {var subQ5=sQuery(id+"F0.wireOp",EDGE,"E27");Q43=makeQuery(id+"F0.imprint","IMPRINT",FACE,{"disambiguationData":[TD([[makeQuery(id+"F0.imprint","IMPRINT",EDGE,{"derivedFrom":subQ5}),-1.0]])]});}
            var Q44;
            {var subQ48=sQuery(id+"F0.wireOp",EDGE,"E27");Q44=makeQuery(id+"F0.imprint","IMPRINT",FACE,{"disambiguationData":[TD([[makeQuery(id+"F0.imprint","IMPRINT",EDGE,{"derivedFrom":subQ48}),1.0]])]});}
            var Q45;
            {var subQ82=sQuery(id+"F0.wireOp",EDGE,"E26");Q45=makeQuery(id+"F0.imprint","IMPRINT",FACE,{"disambiguationData":[TD([[makeQuery(id+"F0.imprint","IMPRINT",EDGE,{"derivedFrom":subQ82}),-1.0]])]});}
            var Q46;
            {var subQ0=sQuery(id+"F0.wireOp",EDGE,"E28.0.1.0");Q46=makeQuery(id+"F0.imprint","IMPRINT",FACE,{"disambiguationData":[TD([[makeQuery(id+"F0.imprint","IMPRINT",EDGE,{"derivedFrom":subQ0}),1.0]])]});}
            var Q47;
            Q47=makeQuery(id+"F0.imprint","IMPRINT",FACE,{"disambiguationData":[TD([[makeQuery(id+"F0.imprint","IMPRINT",EDGE,{"derivedFrom":sQuery(id+"F0.wireOp",EDGE,"E28.1.0.0")}),1.0]])]});
            var Q48;
            Q48=makeQuery(id+"F0.imprint","IMPRINT",FACE,{"disambiguationData":[TD([[makeQuery(id+"F0.imprint","IMPRINT",EDGE,{"derivedFrom":sQuery(id+"F0.wireOp",EDGE,"E28.1.1.0")}),1.0]])]});
            var Q49;
            Q49=makeQuery(id+"F0.imprint","IMPRINT",FACE,{"disambiguationData":[TD([[makeQuery(id+"F0.imprint","IMPRINT",EDGE,{"derivedFrom":sQuery(id+"F0.wireOp",EDGE,"E28.2.0.0")}),1.0]])]});
            var Q50;
            Q50=makeQuery(id+"F0.imprint","IMPRINT",FACE,{"disambiguationData":[TD([[makeQuery(id+"F0.imprint","IMPRINT",EDGE,{"derivedFrom":sQuery(id+"F0.wireOp",EDGE,"E28.2.1.0")}),1.0]])]});
            var Q51;
            Q51=makeQuery(id+"F0.imprint","IMPRINT",FACE,{"disambiguationData":[TD([[makeQuery(id+"F0.imprint","IMPRINT",EDGE,{"derivedFrom":sQuery(id+"F0.wireOp",EDGE,"E29.0.3.0")}),1.0]])]});
            var Q52;
            Q52=makeQuery(id+"F0.imprint","IMPRINT",FACE,{"disambiguationData":[TD([[makeQuery(id+"F0.imprint","IMPRINT",EDGE,{"derivedFrom":sQuery(id+"F0.wireOp",EDGE,"E29.0.3.1")}),1.0]])]});
            var Q53;
            Q53=makeQuery(id+"F0.imprint","IMPRINT",FACE,{"disambiguationData":[TD([[makeQuery(id+"F0.imprint","IMPRINT",EDGE,{"derivedFrom":sQuery(id+"F0.wireOp",EDGE,"E29.0.4.0")}),1.0]])]});
            var Q54;
            Q54=makeQuery(id+"F0.imprint","IMPRINT",FACE,{"disambiguationData":[TD([[makeQuery(id+"F0.imprint","IMPRINT",EDGE,{"derivedFrom":sQuery(id+"F0.wireOp",EDGE,"E29.0.4.1")}),1.0]])]});
            var Q55;
            Q55=makeQuery(id+"F0.imprint","IMPRINT",FACE,{"disambiguationData":[TD([[makeQuery(id+"F0.imprint","IMPRINT",EDGE,{"derivedFrom":sQuery(id+"F0.wireOp",EDGE,"E29.0.5.0")}),1.0]])]});
            var Q56;
            Q56=makeQuery(id+"F0.imprint","IMPRINT",FACE,{"disambiguationData":[TD([[makeQuery(id+"F0.imprint","IMPRINT",EDGE,{"derivedFrom":sQuery(id+"F0.wireOp",EDGE,"E29.0.5.1")}),1.0]])]});
            var Q57;
            Q57=makeQuery(id+"F0.imprint","IMPRINT",FACE,{"disambiguationData":[TD([[makeQuery(id+"F0.imprint","IMPRINT",EDGE,{"derivedFrom":sQuery(id+"F0.wireOp",EDGE,"E29.0.6.0")}),1.0]])]});
            var Q58;
            Q58=makeQuery(id+"F0.imprint","IMPRINT",FACE,{"disambiguationData":[TD([[makeQuery(id+"F0.imprint","IMPRINT",EDGE,{"derivedFrom":sQuery(id+"F0.wireOp",EDGE,"E29.0.6.1")}),1.0]])]});
            var Q59;
            Q59=makeQuery(id+"F0.imprint","IMPRINT",FACE,{"disambiguationData":[TD([[makeQuery(id+"F0.imprint","IMPRINT",EDGE,{"derivedFrom":sQuery(id+"F0.wireOp",EDGE,"E29.0.7.0")}),1.0]])]});
            var Q60;
            Q60=makeQuery(id+"F0.imprint","IMPRINT",FACE,{"disambiguationData":[TD([[makeQuery(id+"F0.imprint","IMPRINT",EDGE,{"derivedFrom":sQuery(id+"F0.wireOp",EDGE,"E29.0.7.1")}),1.0]])]});
            var Q61;
            Q61=makeQuery(id+"F0.imprint","IMPRINT",FACE,{"disambiguationData":[TD([[makeQuery(id+"F0.imprint","IMPRINT",EDGE,{"derivedFrom":sQuery(id+"F0.wireOp",EDGE,"E29.0.8.0")}),1.0]])]});
            var Q62;
            Q62=makeQuery(id+"F0.imprint","IMPRINT",FACE,{"disambiguationData":[TD([[makeQuery(id+"F0.imprint","IMPRINT",EDGE,{"derivedFrom":sQuery(id+"F0.wireOp",EDGE,"E29.0.8.1")}),1.0]])]});
            var Q63;
            Q63=makeQuery(id+"F0.imprint","IMPRINT",FACE,{"disambiguationData":[TD([[makeQuery(id+"F0.imprint","IMPRINT",EDGE,{"derivedFrom":sQuery(id+"F0.wireOp",EDGE,"E29.0.9.0")}),1.0]])]});
            var Q64;
            Q64=makeQuery(id+"F0.imprint","IMPRINT",FACE,{"disambiguationData":[TD([[makeQuery(id+"F0.imprint","IMPRINT",EDGE,{"derivedFrom":sQuery(id+"F0.wireOp",EDGE,"E29.0.9.1")}),1.0]])]});
            var Q65;
            Q65=makeQuery(id+"F0.imprint","IMPRINT",FACE,{"disambiguationData":[TD([[makeQuery(id+"F0.imprint","IMPRINT",EDGE,{"derivedFrom":sQuery(id+"F0.wireOp",EDGE,"E29.0.10.0")}),1.0]])]});
            var Q66;
            Q66=makeQuery(id+"F0.imprint","IMPRINT",FACE,{"disambiguationData":[TD([[makeQuery(id+"F0.imprint","IMPRINT",EDGE,{"derivedFrom":sQuery(id+"F0.wireOp",EDGE,"E29.0.10.1")}),1.0]])]});
            var Q67;
            Q67=makeQuery(id+"F0.imprint","IMPRINT",FACE,{"disambiguationData":[TD([[makeQuery(id+"F0.imprint","IMPRINT",EDGE,{"derivedFrom":sQuery(id+"F0.wireOp",EDGE,"E29.0.11.0")}),1.0]])]});
            var Q68;
            Q68=makeQuery(id+"F0.imprint","IMPRINT",FACE,{"disambiguationData":[TD([[makeQuery(id+"F0.imprint","IMPRINT",EDGE,{"derivedFrom":sQuery(id+"F0.wireOp",EDGE,"E29.0.11.1")}),1.0]])]});
            var Q69;
            Q69=makeQuery(id+"F0.imprint","IMPRINT",FACE,{"disambiguationData":[TD([[makeQuery(id+"F0.imprint","IMPRINT",EDGE,{"derivedFrom":sQuery(id+"F0.wireOp",EDGE,"E29.0.12.0")}),1.0]])]});
            var Q70;
            Q70=makeQuery(id+"F0.imprint","IMPRINT",FACE,{"disambiguationData":[TD([[makeQuery(id+"F0.imprint","IMPRINT",EDGE,{"derivedFrom":sQuery(id+"F0.wireOp",EDGE,"E29.0.12.1")}),1.0]])]});
            var Q71;
            Q71=makeQuery(id+"F0.imprint","IMPRINT",FACE,{"disambiguationData":[TD([[makeQuery(id+"F0.imprint","IMPRINT",EDGE,{"derivedFrom":sQuery(id+"F0.wireOp",EDGE,"E29.0.13.0")}),1.0]])]});
            var Q72;
            Q72=makeQuery(id+"F0.imprint","IMPRINT",FACE,{"disambiguationData":[TD([[makeQuery(id+"F0.imprint","IMPRINT",EDGE,{"derivedFrom":sQuery(id+"F0.wireOp",EDGE,"E29.0.13.1")}),1.0]])]});
            var Q73;
            Q73=makeQuery(id+"F0.imprint","IMPRINT",FACE,{"disambiguationData":[TD([[makeQuery(id+"F0.imprint","IMPRINT",EDGE,{"derivedFrom":sQuery(id+"F0.wireOp",EDGE,"E29.0.14.0")}),1.0]])]});
            var Q74;
            Q74=makeQuery(id+"F0.imprint","IMPRINT",FACE,{"disambiguationData":[TD([[makeQuery(id+"F0.imprint","IMPRINT",EDGE,{"derivedFrom":sQuery(id+"F0.wireOp",EDGE,"E29.0.14.1")}),1.0]])]});
            var Q75;
            Q75=makeQuery(id+"F0.imprint","IMPRINT",FACE,{"disambiguationData":[TD([[makeQuery(id+"F0.imprint","IMPRINT",EDGE,{"derivedFrom":sQuery(id+"F0.wireOp",EDGE,"E29.0.15.0")}),1.0]])]});
            var Q76;
            Q76=makeQuery(id+"F0.imprint","IMPRINT",FACE,{"disambiguationData":[TD([[makeQuery(id+"F0.imprint","IMPRINT",EDGE,{"derivedFrom":sQuery(id+"F0.wireOp",EDGE,"E29.0.15.1")}),1.0]])]});
            var Q77;
            Q77=makeQuery(id+"F0.imprint","IMPRINT",FACE,{"disambiguationData":[TD([[makeQuery(id+"F0.imprint","IMPRINT",EDGE,{"derivedFrom":sQuery(id+"F0.wireOp",EDGE,"E29.0.16.0")}),1.0]])]});
            var Q78;
            Q78=makeQuery(id+"F0.imprint","IMPRINT",FACE,{"disambiguationData":[TD([[makeQuery(id+"F0.imprint","IMPRINT",EDGE,{"derivedFrom":sQuery(id+"F0.wireOp",EDGE,"E29.0.16.1")}),1.0]])]});
            var Q79;
            Q79=makeQuery(id+"F0.imprint","IMPRINT",FACE,{"disambiguationData":[TD([[makeQuery(id+"F0.imprint","IMPRINT",EDGE,{"derivedFrom":sQuery(id+"F0.wireOp",EDGE,"E29.0.17.0")}),1.0]])]});
            var Q80;
            Q80=makeQuery(id+"F0.imprint","IMPRINT",FACE,{"disambiguationData":[TD([[makeQuery(id+"F0.imprint","IMPRINT",EDGE,{"derivedFrom":sQuery(id+"F0.wireOp",EDGE,"E29.0.17.1")}),1.0]])]});
            var Q81;
            Q81=makeQuery(id+"F0.imprint","IMPRINT",FACE,{"disambiguationData":[TD([[makeQuery(id+"F0.imprint","IMPRINT",EDGE,{"derivedFrom":sQuery(id+"F0.wireOp",EDGE,"E29.0.18.0")}),1.0]])]});
            var Q82;
            Q82=makeQuery(id+"F0.imprint","IMPRINT",FACE,{"disambiguationData":[TD([[makeQuery(id+"F0.imprint","IMPRINT",EDGE,{"derivedFrom":sQuery(id+"F0.wireOp",EDGE,"E29.0.18.1")}),1.0]])]});
            extrude(context, id + "F3", {"entities" : qUnion([Q0, Q1, Q2, Q3, Q4, Q5, Q6, Q7, Q8, Q9, Q10, Q11, Q12, Q13, Q14, Q15, Q16, Q17, Q18, Q19, Q20, Q21, Q22, Q23, Q24, Q25, Q26, Q27, Q28, Q29, Q30, Q31, Q32, Q33, Q34, Q35, Q36, Q37, Q38, Q39, Q40, Q41, Q42, Q43, Q44, Q45, Q46, Q47, Q48, Q49, Q50, Q51, Q52, Q53, Q54, Q55, Q56, Q57, Q58, Q59, Q60, Q61, Q62, Q63, Q64, Q65, Q66, Q67, Q68, Q69, Q70, Q71, Q72, Q73, Q74, Q75, Q76, Q77, Q78, Q79, Q80, Q81, Q82]), "operationType" : NewBodyOperationType.ADD, "oppositeDirection" : true, "depth" : 3.2 * mm, "offsetDistance" : 25 * mm});
        }
        {
            var Q0;
            Q0=makeQuery(id+"F1.opExtrude","CAP_EDGE",EDGE,{"disambiguationData":[OSD([sQuery(id+"F0.wireOp",EDGE,"E8")])],"isStart":false});
            fillet(context, id + "F4", {"entities" : qUnion([Q0]), "tangentPropagation" : true, "radius" : .8 * mm, "defaultsChanged" : true, "vertexSettings" : [], "allowEdgeOverflow" : false});
        }
    });
